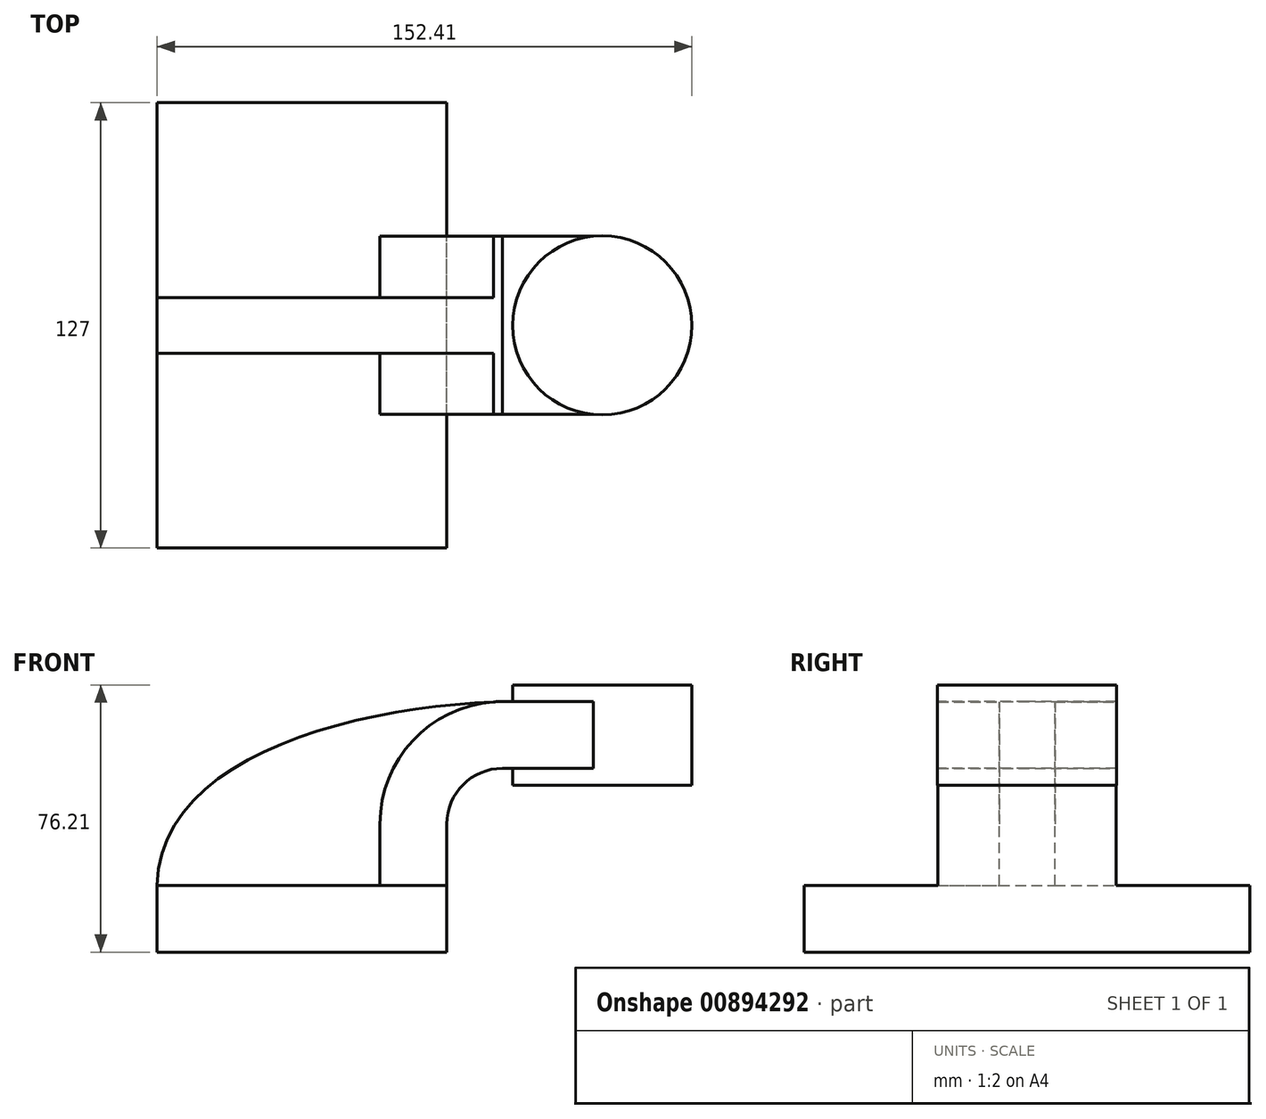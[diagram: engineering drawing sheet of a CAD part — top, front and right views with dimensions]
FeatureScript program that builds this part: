
annotation { "Feature Type Name" : "Feature", "Feature Type Description" : "" }
export const myFeature = defineFeature(function(context is Context, id is Id, definition is map)
    precondition{}
    {
        {
            var Q0;
            Q0=qCreatedBy(makeId("Front.planeOp"),FACE);
            var sketch = newSketch(context, id + "F0", { "sketchPlane" : qUnion([Q0])});
            skLineSegment(sketch, "E0.bottom", {"start": v(-41.28, 9.52) * mm, "end": v(41.28, 9.53) * mm});
            skLineSegment(sketch, "E0.top", {"start": v(-41.28, -9.53) * mm, "end": v(41.28, -9.53) * mm});
            skLineSegment(sketch, "E0.left", {"start": v(-41.28, 9.52) * mm, "end": v(-41.28, -9.53) * mm});
            skLineSegment(sketch, "E0.right", {"start": v(41.28, 9.53) * mm, "end": v(41.28, -9.52) * mm});
            skPoint(sketch, "E0.middle", {"position": v(0, 0) * mm});
            skLineSegment(sketch, "E1.bottom", {"start": v(111.12, 66.68) * mm, "end": v(60.32, 66.68) * mm});
            skLineSegment(sketch, "E1.top", {"start": v(111.12, 38.1) * mm, "end": v(60.32, 38.1) * mm});
            skLineSegment(sketch, "E1.left", {"start": v(111.12, 66.68) * mm, "end": v(111.12, 38.1) * mm});
            skLineSegment(sketch, "E1.right", {"start": v(60.32, 66.68) * mm, "end": v(60.32, 38.1) * mm});
            skPoint(sketch, "E1.middle", {"position": v(85.72, 52.39) * mm});
            skLineSegment(sketch, "E2", {"start": v(41.27, 9.53) * mm, "end": v(41.27, 27) * mm});
            skArc(sketch, "E3", {"start": v(41.27, 27) * mm, "mid": v(45.92, 38.23) * mm, "end": v(57.15, 42.88) * mm});
            skLineSegment(sketch, "E4", {"start": v(57.15, 42.88) * mm, "end": v(85.6, 42.88) * mm});
            skLineSegment(sketch, "E5.0", {"start": v(57.15, 61.93) * mm, "end": v(85.6, 61.93) * mm});
            skArc(sketch, "E5.1", {"start": v(22.23, 27) * mm, "mid": v(32.45, 51.7) * mm, "end": v(57.15, 61.93) * mm});
            skLineSegment(sketch, "E5.2", {"start": v(22.22, 9.53) * mm, "end": v(22.22, 27) * mm});
            skLineSegment(sketch, "E6", {"start": v(85.6, 38.1) * mm, "end": v(85.6, 66.68) * mm});
            skPoint(sketch, "E6.endSnap0", {"position": v(85.72, 66.68) * mm});
            skFitSpline(sketch, "E7", {"points": [v(-41.28, 9.53) * mm, v(57.15, 61.93) * mm], "startDerivative": vector(2.47, 111.8) * mm, "endDerivative": vector(123.6, 3.77) * mm});
            skSolve(sketch);
        }
        {
            var Q0;
            Q0=makeQuery(id+"F0.imprint","IMPRINT",FACE,{"disambiguationData":[TD([[makeQuery(id+"F0.imprint","IMPRINT",EDGE,{"derivedFrom":sQuery(id+"F0.wireOp",EDGE,"E0.top")}),1.0]])]});
            extrude(context, id + "F1", {"entities" : qUnion([Q0]), "endBound" : BoundingType.SYMMETRIC, "depth" : 127 * mm, "offsetDistance" : 25.4 * mm});
        }
        {
            var Q0;
            {var subQ1=sQuery(id+"F0.wireOp",EDGE,"E2");Q0=makeQuery(id+"F0.imprint","IMPRINT",FACE,{"disambiguationData":[TD([[makeQuery(id+"F0.imprint","IMPRINT",EDGE,{"derivedFrom":subQ1}),1.0]])]});}
            var Q1;
            {var subQ0=sQuery(id+"F0.wireOp",EDGE,"E5.0");var subQ1=sQuery(id+"F0.wireOp",EDGE,"E1.right");var subQ2=makeQuery(id+"F0.imprint","INTERSECT",VERTEX,{"derivedFrom":[subQ1,subQ0]});Q1=makeQuery(id+"F0.imprint","IMPRINT",FACE,{"disambiguationData":[TD([[makeQuery(id+"F0.imprint","IMPRINT",EDGE,{"disambiguationData":[TD([[subQ2,-1.0]])],"derivedFrom":subQ1}),1.0]])]});}
            extrude(context, id + "F2", {"entities" : qUnion([Q0, Q1]), "operationType" : NewBodyOperationType.ADD, "endBound" : BoundingType.SYMMETRIC, "depth" : 50.8 * mm, "offsetDistance" : 25.4 * mm});
        }
        {
            var Q0;
            {var subQ3=sQuery(id+"F0.wireOp",EDGE,"E5.2");Q0=makeQuery(id+"F0.imprint","IMPRINT",FACE,{"disambiguationData":[TD([[makeQuery(id+"F0.imprint","IMPRINT",EDGE,{"derivedFrom":subQ3}),1.0]])]});}
            extrude(context, id + "F3", {"entities" : qUnion([Q0]), "operationType" : NewBodyOperationType.ADD, "endBound" : BoundingType.SYMMETRIC, "depth" : 15.88 * mm, "offsetDistance" : 25.4 * mm});
        }
        {
            var Q0;
            {var subQ0=sQuery(id+"F0.wireOp",EDGE,"E1.left");Q0=makeQuery(id+"F0.imprint","IMPRINT",FACE,{"disambiguationData":[TD([[makeQuery(id+"F0.imprint","IMPRINT",EDGE,{"derivedFrom":subQ0}),-1.0]])]});}
            var Q1;
            Q1=sQuery(id+"F0.wireOp",EDGE,"E6");
            revolve(context, id + "F4", {"operationType" : NewBodyOperationType.ADD, "surfaceOperationType" : NewSurfaceOperationType.NEW, "entities" : qUnion([Q0]), "axis" : qUnion([Q1]), "revolveType" : RevolveType.FULL});
        }
    });
